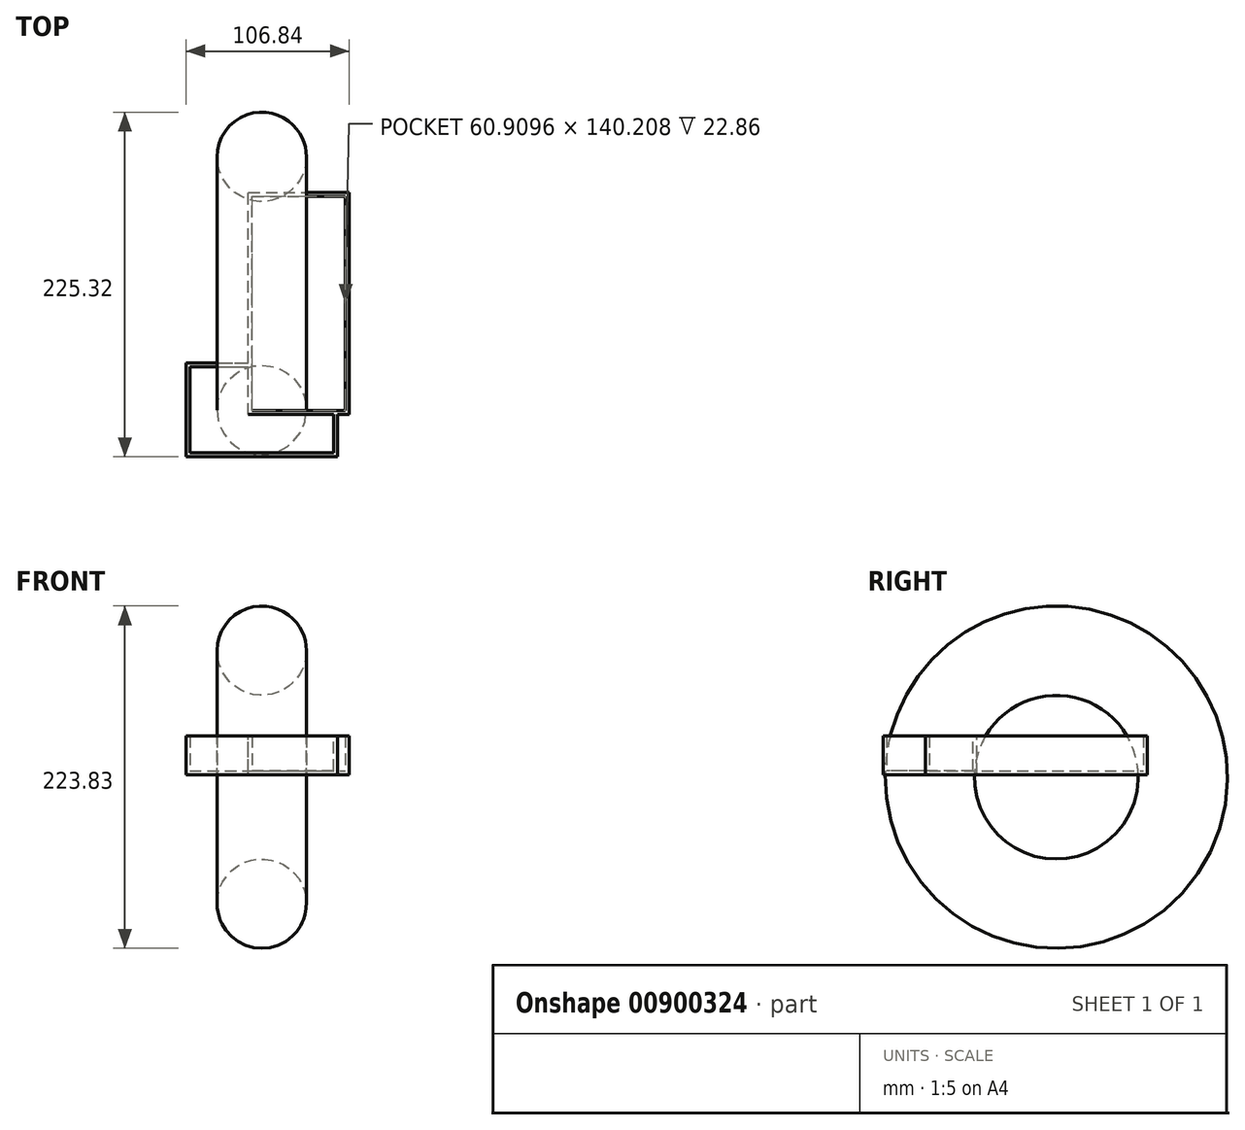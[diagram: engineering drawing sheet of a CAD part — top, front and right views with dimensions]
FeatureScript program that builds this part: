
annotation { "Feature Type Name" : "Feature", "Feature Type Description" : "" }
export const myFeature = defineFeature(function(context is Context, id is Id, definition is map)
    precondition{}
    {
        {
            var Q0;
            Q0=qCreatedBy(makeId("Top.planeOp"),FACE);
            var sketch = newSketch(context, id + "F0", { "sketchPlane" : qUnion([Q0])});
            skLineSegment(sketch, "E0.bottom", {"start": v(-49.58, 30.7) * mm, "end": v(49.58, 30.7) * mm});
            skLineSegment(sketch, "E0.top", {"start": v(-49.58, -30.7) * mm, "end": v(49.58, -30.7) * mm});
            skLineSegment(sketch, "E0.left", {"start": v(-49.58, 30.7) * mm, "end": v(-49.58, -30.7) * mm});
            skLineSegment(sketch, "E0.right", {"start": v(49.58, 30.7) * mm, "end": v(49.58, -30.7) * mm});
            skPoint(sketch, "E0.middle", {"position": v(0, 0) * mm});
            skSolve(sketch);
        }
        {
            var Q0;
            Q0=makeQuery(id+"F0.imprint","IMPRINT",FACE,{"disambiguationData":[TD([[makeQuery(id+"F0.imprint","IMPRINT",EDGE,{"derivedFrom":sQuery(id+"F0.wireOp",EDGE,"E0.bottom")}),-1.0]])]});
            extrude(context, id + "F1", {"entities" : qUnion([Q0]), "depth" : 25.4 * mm, "offsetDistance" : 25.4 * mm});
        }
        {
            var Q0;
            Q0=makeQuery(id+"F1.opExtrude","CAP_FACE",FACE,{"disambiguationData":[OSD([sQuery(id+"F0.wireOp",EDGE,"E0.bottom"),sQuery(id+"F0.wireOp",EDGE,"E0.top"),sQuery(id+"F0.wireOp",EDGE,"E0.left"),sQuery(id+"F0.wireOp",EDGE,"E0.right")])],"isStart":false});
            shell(context, id + "F2", {"entities" : qUnion([Q0]), "thickness" : 2.54 * mm});
        }
        {
            var Q0;
            Q0=qCreatedBy(makeId("Top.planeOp"),FACE);
            var sketch = newSketch(context, id + "F3", { "sketchPlane" : qUnion([Q0])});
            skLineSegment(sketch, "E1.bottom", {"start": v(-8.73, -3.05) * mm, "end": v(57.26, -3.05) * mm});
            skLineSegment(sketch, "E1.top", {"start": v(-8.73, 142.24) * mm, "end": v(57.26, 142.24) * mm});
            skLineSegment(sketch, "E1.left", {"start": v(-8.73, -3.05) * mm, "end": v(-8.73, 142.24) * mm});
            skLineSegment(sketch, "E1.right", {"start": v(57.26, -3.05) * mm, "end": v(57.26, 142.24) * mm});
            skPoint(sketch, "E1.middle", {"position": v(24.26, 69.6) * mm});
            skSolve(sketch);
        }
        {
            var Q0;
            Q0=makeQuery(id+"F3.imprint","IMPRINT",FACE,{"disambiguationData":[TD([[makeQuery(id+"F3.imprint","IMPRINT",EDGE,{"derivedFrom":sQuery(id+"F3.wireOp",EDGE,"E1.bottom")}),1.0]])]});
            extrude(context, id + "F4", {"entities" : qUnion([Q0]), "operationType" : NewBodyOperationType.ADD, "depth" : 25.4 * mm, "offsetDistance" : 25.4 * mm});
        }
        {
            var Q0;
            Q0=makeQuery(id+"F4.boolean.opBoolean","MERGE",FACE,{"derivedFrom":[makeQuery(id+"F1.opExtrude","CAP_FACE",FACE,{"disambiguationData":[OSD([sQuery(id+"F0.wireOp",EDGE,"E0.bottom"),sQuery(id+"F0.wireOp",EDGE,"E0.top"),sQuery(id+"F0.wireOp",EDGE,"E0.left"),sQuery(id+"F0.wireOp",EDGE,"E0.right")])],"isStart":false}),makeQuery(id+"F4.opExtrude","CAP_FACE",FACE,{"disambiguationData":[OSD([sQuery(id+"F3.wireOp",EDGE,"E1.bottom"),sQuery(id+"F3.wireOp",EDGE,"E1.top"),sQuery(id+"F3.wireOp",EDGE,"E1.left"),sQuery(id+"F3.wireOp",EDGE,"E1.right")])],"isStart":false})]});
            shell(context, id + "F5", {"entities" : qUnion([Q0]), "thickness" : 2.54 * mm});
        }
        {
            var Q0;
            Q0=makeQuery(id+"F1.opExtrude","SWEPT_BODY",BODY,{"disambiguationData":[OSD([sQuery(id+"F0.wireOp",EDGE,"E0.bottom"),sQuery(id+"F0.wireOp",EDGE,"E0.top"),sQuery(id+"F0.wireOp",EDGE,"E0.left"),sQuery(id+"F0.wireOp",EDGE,"E0.right")])]});
            transform(context, id + "F6", {"entities" : qUnion([Q0]), "transformType" : TransformType.TRANSLATION_3D, "dx" : 0 * mm, "dy" : 65.53 * mm, "dz" : 0 * mm, "makeCopy" : true});
        }
        {
            var Q0;
            Q0=makeQuery(id+"F6.opPattern","COPY",BODY,{"derivedFrom":makeQuery(id+"F1.opExtrude","SWEPT_BODY",BODY,{"disambiguationData":[OSD([sQuery(id+"F0.wireOp",EDGE,"E0.bottom"),sQuery(id+"F0.wireOp",EDGE,"E0.top"),sQuery(id+"F0.wireOp",EDGE,"E0.left"),sQuery(id+"F0.wireOp",EDGE,"E0.right")])]}),"instanceName":"1"});
            deleteBodies(context, id + "F7", {"entities" : qUnion([Q0])});
        }
        {
            var Q0;
            Q0=qCreatedBy(makeId("Top.planeOp"),FACE);
            var sketch = newSketch(context, id + "F8", { "sketchPlane" : qUnion([Q0])});
            skCircle(sketch, "E2", {"center": v(0, 0) * mm, "radius": 29.2 * mm});
            skSolve(sketch);
        }
        {
            var Q0;
            Q0=qCreatedBy(makeId("Right.planeOp"),FACE);
            var sketch = newSketch(context, id + "F9", { "sketchPlane" : qUnion([Q0])});
            skCircle(sketch, "E3", {"center": v(82.7, -1.53) * mm, "radius": 82.72 * mm});
            skPoint(sketch, "E3.first.point", {"position": v(0, 0) * mm});
            skPoint(sketch, "E3.second.point", {"position": v(0, 0) * mm});
            skPoint(sketch, "E3.third.point", {"position": v(87.98, -84.07) * mm});
            skSolve(sketch);
        }
        {
            var Q0;
            Q0=makeQuery(id+"F8.imprint","IMPRINT",FACE,{"disambiguationData":[TD([[makeQuery(id+"F8.imprint","IMPRINT",EDGE,{"derivedFrom":sQuery(id+"F8.wireOp",EDGE,"E2")}),1.0]])]});
            var Q1;
            Q1=sQuery(id+"F9.wireOp",EDGE,"E3");
            sweep(context, id + "F10", {"profiles" : qUnion([Q0]), "path" : qUnion([Q1])});
        }
    });
